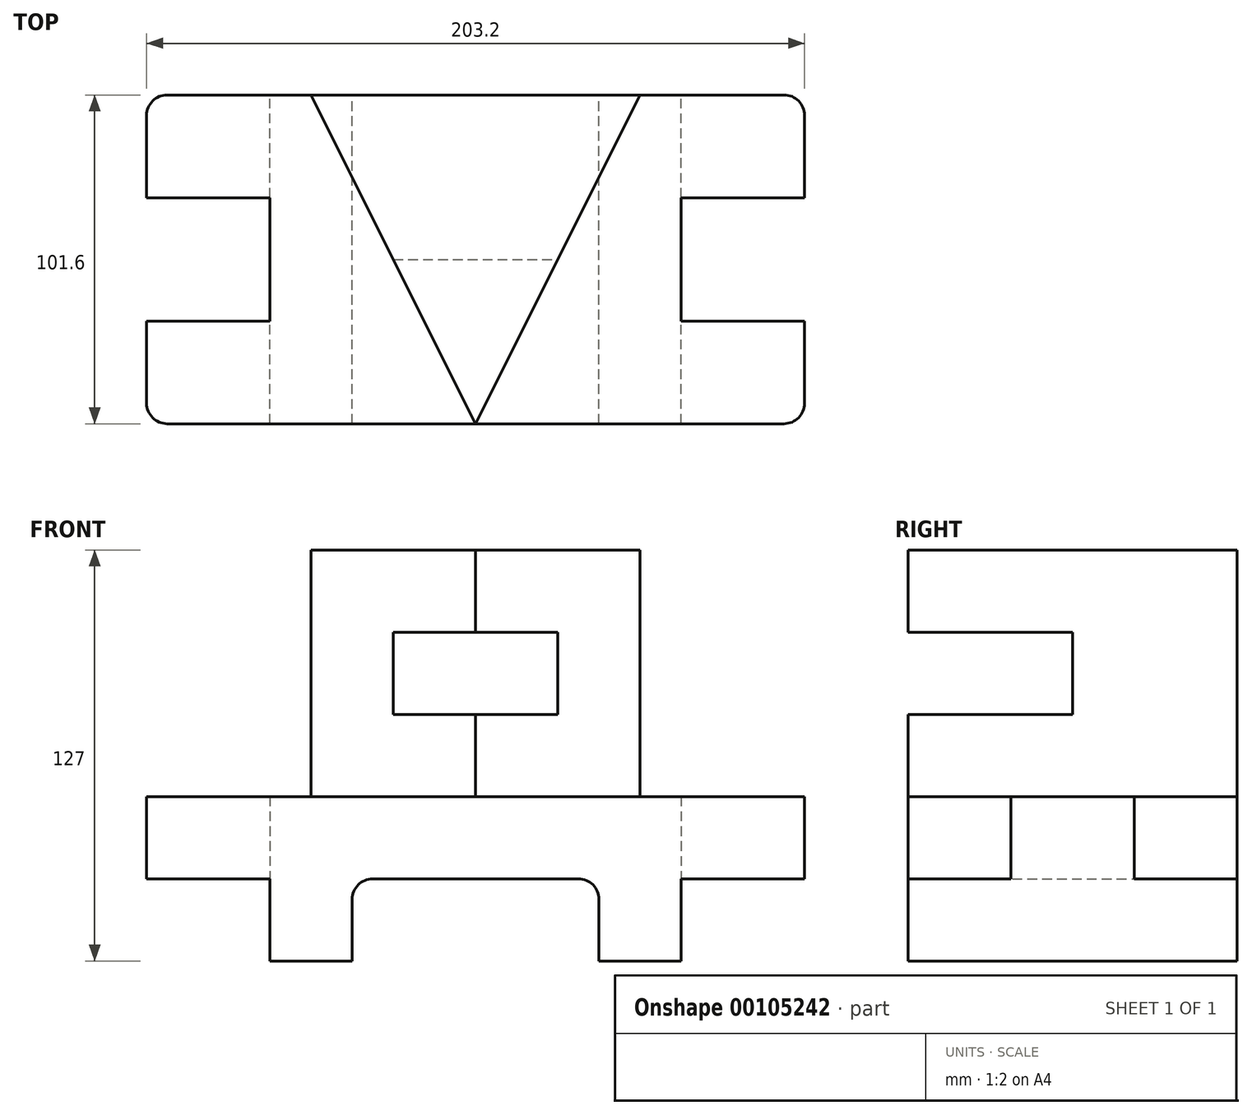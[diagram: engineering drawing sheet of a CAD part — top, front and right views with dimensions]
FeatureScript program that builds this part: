
annotation { "Feature Type Name" : "Feature", "Feature Type Description" : "" }
export const myFeature = defineFeature(function(context is Context, id is Id, definition is map)
    precondition{}
    {
        {
            var Q0;
            Q0=qCreatedBy(makeId("Front.planeOp"),FACE);
            var sketch = newSketch(context, id + "F0", { "sketchPlane" : qUnion([Q0])});
            skLineSegment(sketch, "E0", {"start": v(0, 0) * mm, "end": v(25.4, 0) * mm});
            skLineSegment(sketch, "E1", {"start": v(25.4, 0) * mm, "end": v(25.4, 25.4) * mm});
            skLineSegment(sketch, "E2", {"start": v(25.4, 25.4) * mm, "end": v(101.6, 25.4) * mm});
            skLineSegment(sketch, "E3", {"start": v(101.6, 25.4) * mm, "end": v(101.6, 0) * mm});
            skLineSegment(sketch, "E4", {"start": v(101.6, 0) * mm, "end": v(127, 0) * mm});
            skLineSegment(sketch, "E5", {"start": v(127, 0) * mm, "end": v(127, 25.4) * mm});
            skLineSegment(sketch, "E6", {"start": v(127, 25.4) * mm, "end": v(165.1, 25.4) * mm});
            skLineSegment(sketch, "E7", {"start": v(165.1, 25.4) * mm, "end": v(165.1, 50.8) * mm});
            skLineSegment(sketch, "E8", {"start": v(165.1, 50.8) * mm, "end": v(-38.1, 50.8) * mm});
            skLineSegment(sketch, "E9", {"start": v(-38.1, 50.8) * mm, "end": v(-38.1, 25.4) * mm});
            skLineSegment(sketch, "E10", {"start": v(-38.1, 25.4) * mm, "end": v(0, 25.4) * mm});
            skLineSegment(sketch, "E11", {"start": v(0, 25.4) * mm, "end": v(0, 0) * mm});
            skSolve(sketch);
        }
        {
            var Q0;
            Q0 = qSketchRegion(id + "F0", true);
            extrude(context, id + "F1", {"entities" : qUnion([Q0]), "endBound" : BoundingType.SYMMETRIC, "depth" : 101.6 * mm});
        }
        {
            var Q0;
            Q0=makeQuery(id+"F1.opExtrude","CAP_EDGE",EDGE,{"disambiguationData":[OSD([sQuery(id+"F0.wireOp",EDGE,"E7")])],"isStart":false});
            var Q1;
            Q1=makeQuery(id+"F1.opExtrude","CAP_EDGE",EDGE,{"disambiguationData":[OSD([sQuery(id+"F0.wireOp",EDGE,"E7")])],"isStart":true});
            var Q2;
            Q2=makeQuery(id+"F1.opExtrude","CAP_EDGE",EDGE,{"disambiguationData":[OSD([sQuery(id+"F0.wireOp",EDGE,"E9")])],"isStart":false});
            var Q3;
            Q3=makeQuery(id+"F1.opExtrude","CAP_EDGE",EDGE,{"disambiguationData":[OSD([sQuery(id+"F0.wireOp",EDGE,"E9")])],"isStart":true});
            fillet(context, id + "F2", {"entities" : qUnion([Q0, Q1, Q2, Q3]), "radius" : 6.35 * mm, "tangentPropagation" : true, "allowEdgeOverflow" : false});
        }
        {
            var Q0;
            Q0=makeQuery(id+"F1.opExtrude","SWEPT_EDGE",EDGE,{"disambiguationData":[OSD([sQuery(id+"F0.wireOp",EDGE,"E1"),sQuery(id+"F0.wireOp",EDGE,"E2")])]});
            var Q1;
            Q1=makeQuery(id+"F1.opExtrude","SWEPT_EDGE",EDGE,{"disambiguationData":[OSD([sQuery(id+"F0.wireOp",EDGE,"E2"),sQuery(id+"F0.wireOp",EDGE,"E3")])]});
            fillet(context, id + "F3", {"entities" : qUnion([Q0, Q1]), "radius" : 6.35 * mm, "tangentPropagation" : true, "allowEdgeOverflow" : false});
        }
        {
            var Q0;
            Q0=makeQuery(id+"F1.opExtrude","SWEPT_FACE",FACE,{"disambiguationData":[OSD([sQuery(id+"F0.wireOp",EDGE,"E7")])]});
            var sketch = newSketch(context, id + "F4", { "sketchPlane" : qUnion([Q0])});
            skLineSegment(sketch, "E12.bottom", {"start": v(-19.05, 50.8) * mm, "end": v(19.05, 50.8) * mm});
            skLineSegment(sketch, "E12.top", {"start": v(-19.05, 25.4) * mm, "end": v(19.05, 25.4) * mm});
            skLineSegment(sketch, "E12.left", {"start": v(-19.05, 50.8) * mm, "end": v(-19.05, 25.4) * mm});
            skLineSegment(sketch, "E12.right", {"start": v(19.05, 50.8) * mm, "end": v(19.05, 25.4) * mm});
            skSolve(sketch);
        }
        {
            var Q0;
            Q0=makeQuery(id+"F4.imprint","IMPRINT",FACE,{"disambiguationData":[TD([[makeQuery(id+"F4.imprint","IMPRINT",EDGE,{"derivedFrom":sQuery(id+"F4.wireOp",EDGE,"E12.bottom")}),-1.0]])]});
            extrude(context, id + "F5", {"entities" : qUnion([Q0]), "operationType" : NewBodyOperationType.REMOVE, "oppositeDirection" : true, "depth" : 38.1 * mm});
        }
        {
            var Q0;
            Q0=qCreatedBy(makeId("Right.planeOp"),FACE);
            var sketch = newSketch(context, id + "F6", { "sketchPlane" : qUnion([Q0])});
            skLineSegment(sketch, "E13.bottom", {"start": v(19.05, 50.8) * mm, "end": v(-19.05, 50.8) * mm});
            skLineSegment(sketch, "E13.top", {"start": v(19.05, 25.4) * mm, "end": v(-19.05, 25.4) * mm});
            skLineSegment(sketch, "E13.left", {"start": v(19.05, 50.8) * mm, "end": v(19.05, 25.4) * mm});
            skLineSegment(sketch, "E13.right", {"start": v(-19.05, 50.8) * mm, "end": v(-19.05, 25.4) * mm});
            skSolve(sketch);
        }
        {
            var Q0;
            Q0 = qSketchRegion(id + "F6", true);
            var Q1;
            Q1 = qSketchRegion(id + "FBSQIxX4l9AH8cj_1", true);
            extrude(context, id + "F7", {"entities" : qUnion([Q0, Q1]), "operationType" : NewBodyOperationType.REMOVE, "oppositeDirection" : true, "depth" : 38.1 * mm});
        }
        {
            var Q0;
            Q0=makeQuery(id+"F1.opExtrude","SWEPT_FACE",FACE,{"disambiguationData":[OSD([sQuery(id+"F0.wireOp",EDGE,"E8")])]});
            var sketch = newSketch(context, id + "F8", { "sketchPlane" : qUnion([Q0])});
            skLineSegment(sketch, "E14.bottom", {"start": v(12.7, 50.8) * mm, "end": v(114.3, 50.8) * mm});
            skLineSegment(sketch, "E14.top", {"start": v(12.7, -50.8) * mm, "end": v(114.3, -50.8) * mm});
            skLineSegment(sketch, "E14.left", {"start": v(12.7, 50.8) * mm, "end": v(12.7, -50.8) * mm});
            skLineSegment(sketch, "E14.right", {"start": v(114.3, 50.8) * mm, "end": v(114.3, -50.8) * mm});
            skSolve(sketch);
        }
        {
            var Q0;
            Q0=makeQuery(id+"F8.imprint","IMPRINT",FACE,{"disambiguationData":[TD([[makeQuery(id+"F8.imprint","IMPRINT",EDGE,{"derivedFrom":sQuery(id+"F8.wireOp",EDGE,"E14.bottom")}),1.0]])]});
            extrude(context, id + "F9", {"entities" : qUnion([Q0]), "operationType" : NewBodyOperationType.ADD, "depth" : 76.2 * mm});
        }
        {
            var Q0;
            Q0=makeQuery(id+"F9.opExtrude","SWEPT_FACE",FACE,{"disambiguationData":[OSD([sQuery(id+"F8.wireOp",EDGE,"E14.right")])]});
            var sketch = newSketch(context, id + "F10", { "sketchPlane" : qUnion([Q0])});
            skLineSegment(sketch, "E15.bottom", {"start": v(-50.8, 101.6) * mm, "end": v(0, 101.6) * mm});
            skLineSegment(sketch, "E15.top", {"start": v(-50.8, 76.2) * mm, "end": v(0, 76.2) * mm});
            skLineSegment(sketch, "E15.left", {"start": v(-50.8, 101.6) * mm, "end": v(-50.8, 76.2) * mm});
            skLineSegment(sketch, "E15.right", {"start": v(0, 101.6) * mm, "end": v(0, 76.2) * mm});
            skSolve(sketch);
        }
        {
            var Q0;
            Q0 = qSketchRegion(id + "F10", true);
            extrude(context, id + "F11", {"entities" : qUnion([Q0]), "operationType" : NewBodyOperationType.REMOVE, "endBound" : BoundingType.THROUGH_ALL, "oppositeDirection" : true, "depth" : 25.4 * mm});
        }
        {
            var Q0;
            Q0=makeQuery(id+"F9.opExtrude","CAP_FACE",FACE,{"disambiguationData":[OSD([sQuery(id+"F8.wireOp",EDGE,"E14.bottom"),sQuery(id+"F8.wireOp",EDGE,"E14.top"),sQuery(id+"F8.wireOp",EDGE,"E14.left"),sQuery(id+"F8.wireOp",EDGE,"E14.right")])],"isStart":false});
            var sketch = newSketch(context, id + "F12", { "sketchPlane" : qUnion([Q0])});
            skLineSegment(sketch, "E16", {"start": v(63.5, -50.8) * mm, "end": v(12.7, 50.8) * mm});
            skLineSegment(sketch, "E17", {"start": v(12.7, 50.8) * mm, "end": v(114.3, 50.8) * mm});
            skLineSegment(sketch, "E18", {"start": v(114.3, 50.8) * mm, "end": v(63.5, -50.8) * mm});
            skSolve(sketch);
        }
        {
            var Q0;
            {var subQ0=sQuery(id+"F12.wireOp",EDGE,"E16");Q0=makeQuery(id+"F12.imprint","IMPRINT",FACE,{"disambiguationData":[TD([[makeQuery(id+"F12.imprint","IMPRINT",EDGE,{"derivedFrom":subQ0}),1.0]])]});}
            var Q1;
            {var subQ0=sQuery(id+"F0.wireOp",EDGE,"E9");var subQ5=sQuery(id+"F0.wireOp",EDGE,"E8");Q1=makeQuery(id+"F9.boolean.opBoolean","SPLIT",FACE,{"disambiguationData":[TD([makeQuery(id+"F1.opExtrude","SWEPT_FACE",FACE,{"disambiguationData":[OSD([subQ0])]})])],"derivedFrom":makeQuery(id+"F1.opExtrude","SWEPT_FACE",FACE,{"disambiguationData":[OSD([subQ5])]})});}
            extrude(context, id + "F13", {"entities" : qUnion([Q0]), "operationType" : NewBodyOperationType.REMOVE, "endBound" : BoundingType.UP_TO_SURFACE, "oppositeDirection" : true, "endBoundEntityFace" : qUnion([Q1]), "depth" : 25.4 * mm});
        }
        {
            var Q0;
            {var subQ0=sQuery(id+"F12.wireOp",EDGE,"E18");Q0=makeQuery(id+"F12.imprint","IMPRINT",FACE,{"disambiguationData":[TD([[makeQuery(id+"F12.imprint","IMPRINT",EDGE,{"derivedFrom":subQ0}),1.0]])]});}
            var Q1;
            {var subQ4=sQuery(id+"F0.wireOp",EDGE,"E8");var subQ7=sQuery(id+"F0.wireOp",EDGE,"E5");Q1=makeQuery(id+"F9.boolean.opBoolean","SPLIT",FACE,{"disambiguationData":[TD([makeQuery(id+"F1.opExtrude","SWEPT_FACE",FACE,{"disambiguationData":[OSD([subQ7])]})])],"derivedFrom":makeQuery(id+"F1.opExtrude","SWEPT_FACE",FACE,{"disambiguationData":[OSD([subQ4])]})});}
            extrude(context, id + "F14", {"entities" : qUnion([Q0]), "operationType" : NewBodyOperationType.REMOVE, "endBound" : BoundingType.UP_TO_SURFACE, "oppositeDirection" : true, "endBoundEntityFace" : qUnion([Q1]), "depth" : 25.4 * mm});
        }
    });
